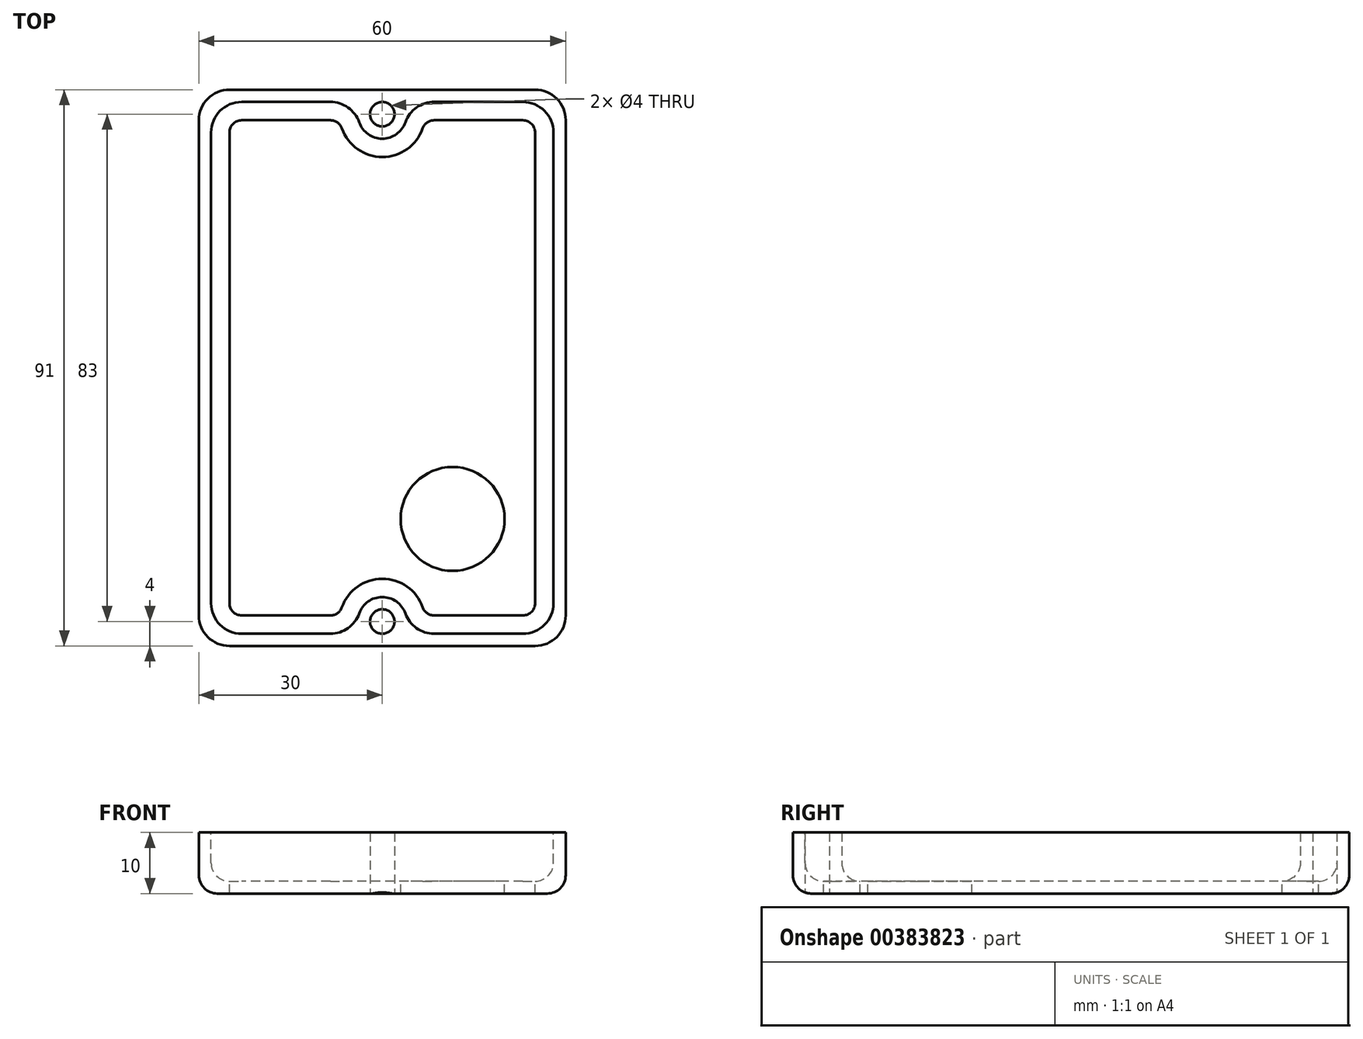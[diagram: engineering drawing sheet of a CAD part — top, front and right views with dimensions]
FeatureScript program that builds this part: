
annotation { "Feature Type Name" : "Feature", "Feature Type Description" : "" }
export const myFeature = defineFeature(function(context is Context, id is Id, definition is map)
    precondition{}
    {
        {
            assignVariable(context, id + "F0", {"name" : "lidwallthickness", "anyValue" : 2});
        }
        {
            assignVariable(context, id + "F1", {"name" : "lidheight", "anyValue" : 10});
        }
        {
            assignVariable(context, id + "F2", {"name" : "filletradius", "anyValue" : 3});
        }
        {
            var Q0;
            Q0=qCreatedBy(makeId("Top.planeOp"),FACE);
            var sketch = newSketch(context, id + "F3", { "sketchPlane" : qUnion([Q0])});
            skLineSegment(sketch, "E0.bottom", {"start": v(30, 45.5) * mm, "end": v(-30, 45.5) * mm});
            skLineSegment(sketch, "E0.top", {"start": v(30, -45.5) * mm, "end": v(-30, -45.5) * mm});
            skLineSegment(sketch, "E0.left", {"start": v(30, 45.5) * mm, "end": v(30, -45.5) * mm});
            skLineSegment(sketch, "E0.right", {"start": v(-30, 45.5) * mm, "end": v(-30, -45.5) * mm});
            skPoint(sketch, "E0.middle", {"position": v(0, 0) * mm});
            skSolve(sketch);
        }
        {
            var Q0;
            Q0=qSketchRegion(id+"F3",true);
            extrude(context, id + "F4", {"entities" : qUnion([Q0]), "depth" : (getVariable(context, 'lidheight')) * mm});
        }
        {
            var Q0;
            Q0=makeQuery(id+"F4.opExtrude","CAP_FACE",FACE,{"disambiguationData":[OSD([sQuery(id+"F3.wireOp",EDGE,"E0.bottom"),sQuery(id+"F3.wireOp",EDGE,"E0.top"),sQuery(id+"F3.wireOp",EDGE,"E0.left"),sQuery(id+"F3.wireOp",EDGE,"E0.right")])],"isStart":false});
            var sketch = newSketch(context, id + "F5", { "sketchPlane" : qUnion([Q0])});
            skLineSegment(sketch, "E1.bottom", {"start": v(28, 43.5) * mm, "end": v(-28, 43.5) * mm});
            skLineSegment(sketch, "E1.top", {"start": v(28, -43.5) * mm, "end": v(-28, -43.5) * mm});
            skLineSegment(sketch, "E1.left", {"start": v(28, 43.5) * mm, "end": v(28, -43.5) * mm});
            skLineSegment(sketch, "E1.right", {"start": v(-28, 43.5) * mm, "end": v(-28, -43.5) * mm});
            skPoint(sketch, "E1.middle", {"position": v(0, 0) * mm});
            skLineSegment(sketch, "E2.bottom", {"start": v(-12, 32.02) * mm, "end": v(12, 32.02) * mm});
            skLineSegment(sketch, "E2.top", {"start": v(-12, 8.02) * mm, "end": v(12, 8.02) * mm});
            skLineSegment(sketch, "E2.left", {"start": v(-12, 32.02) * mm, "end": v(-12, 8.02) * mm});
            skLineSegment(sketch, "E2.right", {"start": v(12, 32.02) * mm, "end": v(12, 8.02) * mm});
            skPoint(sketch, "E2.middle", {"position": v(0, 20.02) * mm});
            skSolve(sketch);
        }
        {
            var Q0;
            Q0=qSketchRegion(id+"F5",true);
            extrude(context, id + "F6", {"entities" : qUnion([Q0]), "operationType" : NewBodyOperationType.REMOVE, "oppositeDirection" : true, "depth" : (getVariable(context, 'lidheight') - getVariable(context, 'lidwallthickness')) * mm});
        }
        {
            var Q0;
            Q0=makeQuery(id+"F4.opExtrude","CAP_FACE",FACE,{"disambiguationData":[OSD([sQuery(id+"F3.wireOp",EDGE,"E0.bottom"),sQuery(id+"F3.wireOp",EDGE,"E0.top"),sQuery(id+"F3.wireOp",EDGE,"E0.left"),sQuery(id+"F3.wireOp",EDGE,"E0.right")])],"isStart":true});
            var sketch = newSketch(context, id + "F7", { "sketchPlane" : qUnion([Q0])});
            skCircle(sketch, "E3", {"center": v(0, -41.5) * mm, "radius": 4 * mm});
            skCircle(sketch, "E4.MirrorC", {"center": v(0, 41.5) * mm, "radius": 4 * mm});
            skSolve(sketch);
        }
        {
            var Q0;
            Q0=qSketchRegion(id+"F7",true);
            extrude(context, id + "F8", {"entities" : qUnion([Q0]), "operationType" : NewBodyOperationType.ADD, "oppositeDirection" : true, "depth" : (getVariable(context, 'lidheight')) * mm});
        }
        {
            var Q0;
            Q0=makeQuery(id+"F4.opExtrude","CAP_FACE",FACE,{"disambiguationData":[OSD([sQuery(id+"F3.wireOp",EDGE,"E0.bottom"),sQuery(id+"F3.wireOp",EDGE,"E0.top"),sQuery(id+"F3.wireOp",EDGE,"E0.left"),sQuery(id+"F3.wireOp",EDGE,"E0.right")])],"isStart":true});
            var sketch = newSketch(context, id + "F9", { "sketchPlane" : qUnion([Q0])});
            skCircle(sketch, "E5", {"center": v(0, -41.5) * mm, "radius": 2 * mm});
            skPoint(sketch, "E5.centerSnap0", {"position": v(0, -45.5) * mm});
            skCircle(sketch, "E6.MirrorC", {"center": v(0, 41.5) * mm, "radius": 2 * mm});
            skSolve(sketch);
        }
        {
            var Q0;
            Q0=qSketchRegion(id+"F9",true);
            extrude(context, id + "F10", {"entities" : qUnion([Q0]), "operationType" : NewBodyOperationType.REMOVE, "endBound" : BoundingType.THROUGH_ALL, "oppositeDirection" : true, "depth" : 25 * mm});
        }
        {
            var Q0;
            Q0=makeQuery(id+"F8.boolean.opBoolean","INTERSECT",EDGE,{"disambiguationData":[OD(1.0)],"derivedFrom":[makeQuery(id+"F6.boolean.opBoolean","COPY",FACE,{"derivedFrom":makeQuery(id+"F6.opExtrude","SWEPT_FACE",FACE,{"disambiguationData":[OSD([sQuery(id+"F5.wireOp",EDGE,"E1.bottom")])]})}),makeQuery(id+"F8.opExtrude","SWEPT_FACE",FACE,{"disambiguationData":[OSD([sQuery(id+"F7.wireOp",EDGE,"E3")])]})]});
            var Q1;
            Q1=makeQuery(id+"F8.boolean.opBoolean","INTERSECT",EDGE,{"disambiguationData":[OD(0.0)],"derivedFrom":[makeQuery(id+"F6.boolean.opBoolean","COPY",FACE,{"derivedFrom":makeQuery(id+"F6.opExtrude","SWEPT_FACE",FACE,{"disambiguationData":[OSD([sQuery(id+"F5.wireOp",EDGE,"E1.bottom")])]})}),makeQuery(id+"F8.opExtrude","SWEPT_FACE",FACE,{"disambiguationData":[OSD([sQuery(id+"F7.wireOp",EDGE,"E3")])]})]});
            var Q2;
            Q2=makeQuery(id+"F8.boolean.opBoolean","INTERSECT",EDGE,{"disambiguationData":[OD(0.0)],"derivedFrom":[makeQuery(id+"F6.boolean.opBoolean","COPY",FACE,{"derivedFrom":makeQuery(id+"F6.opExtrude","SWEPT_FACE",FACE,{"disambiguationData":[OSD([sQuery(id+"F5.wireOp",EDGE,"E1.top")])]})}),makeQuery(id+"F8.opExtrude","SWEPT_FACE",FACE,{"disambiguationData":[OSD([sQuery(id+"F7.wireOp",EDGE,"E4.MirrorC")])]})]});
            var Q3;
            Q3=makeQuery(id+"F8.boolean.opBoolean","INTERSECT",EDGE,{"disambiguationData":[OD(1.0)],"derivedFrom":[makeQuery(id+"F6.boolean.opBoolean","COPY",FACE,{"derivedFrom":makeQuery(id+"F6.opExtrude","SWEPT_FACE",FACE,{"disambiguationData":[OSD([sQuery(id+"F5.wireOp",EDGE,"E1.top")])]})}),makeQuery(id+"F8.opExtrude","SWEPT_FACE",FACE,{"disambiguationData":[OSD([sQuery(id+"F7.wireOp",EDGE,"E4.MirrorC")])]})]});
            fillet(context, id + "F11", {"entities" : qUnion([Q0, Q1, Q2, Q3]), "radius" : 5 * mm, "tangentPropagation" : true, "allowEdgeOverflow" : false});
        }
        {
            var Q0;
            Q0=makeQuery(id+"F4.opExtrude","SWEPT_EDGE",EDGE,{"disambiguationData":[OSD([sQuery(id+"F3.wireOp",EDGE,"E0.top"),sQuery(id+"F3.wireOp",EDGE,"E0.left")])]});
            var Q1;
            Q1=makeQuery(id+"F4.opExtrude","SWEPT_EDGE",EDGE,{"disambiguationData":[OSD([sQuery(id+"F3.wireOp",EDGE,"E0.top"),sQuery(id+"F3.wireOp",EDGE,"E0.right")])]});
            var Q2;
            Q2=makeQuery(id+"F4.opExtrude","SWEPT_EDGE",EDGE,{"disambiguationData":[OSD([sQuery(id+"F3.wireOp",EDGE,"E0.bottom"),sQuery(id+"F3.wireOp",EDGE,"E0.left")])]});
            var Q3;
            Q3=makeQuery(id+"F4.opExtrude","SWEPT_EDGE",EDGE,{"disambiguationData":[OSD([sQuery(id+"F3.wireOp",EDGE,"E0.bottom"),sQuery(id+"F3.wireOp",EDGE,"E0.right")])]});
            var Q4;
            Q4=makeQuery(id+"F6.boolean.opBoolean","COPY",EDGE,{"derivedFrom":makeQuery(id+"F6.opExtrude","SWEPT_EDGE",EDGE,{"disambiguationData":[OSD([sQuery(id+"F5.wireOp",EDGE,"E1.top"),sQuery(id+"F5.wireOp",EDGE,"E1.left")])]})});
            var Q5;
            Q5=makeQuery(id+"F6.boolean.opBoolean","COPY",EDGE,{"derivedFrom":makeQuery(id+"F6.opExtrude","SWEPT_EDGE",EDGE,{"disambiguationData":[OSD([sQuery(id+"F5.wireOp",EDGE,"E1.top"),sQuery(id+"F5.wireOp",EDGE,"E1.right")])]})});
            var Q6;
            Q6=makeQuery(id+"F6.boolean.opBoolean","COPY",EDGE,{"derivedFrom":makeQuery(id+"F6.opExtrude","SWEPT_EDGE",EDGE,{"disambiguationData":[OSD([sQuery(id+"F5.wireOp",EDGE,"E1.bottom"),sQuery(id+"F5.wireOp",EDGE,"E1.right")])]})});
            var Q7;
            Q7=makeQuery(id+"F6.boolean.opBoolean","COPY",EDGE,{"derivedFrom":makeQuery(id+"F6.opExtrude","SWEPT_EDGE",EDGE,{"disambiguationData":[OSD([sQuery(id+"F5.wireOp",EDGE,"E1.bottom"),sQuery(id+"F5.wireOp",EDGE,"E1.left")])]})});
            fillet(context, id + "F12", {"entities" : qUnion([Q0, Q1, Q2, Q3, Q4, Q5, Q6, Q7]), "radius" : 5 * mm, "tangentPropagation" : true, "allowEdgeOverflow" : false});
        }
        {
            var Q0;
            Q0=makeQuery(id+"F6.boolean.opBoolean","COPY",EDGE,{"derivedFrom":makeQuery(id+"F6.opExtrude","CAP_EDGE",EDGE,{"disambiguationData":[OSD([sQuery(id+"F5.wireOp",EDGE,"E1.right")])],"isStart":false})});
            var Q1;
            Q1=makeQuery(id+"F4.opExtrude","CAP_EDGE",EDGE,{"disambiguationData":[OSD([sQuery(id+"F3.wireOp",EDGE,"E0.left")])],"isStart":true});
            fillet(context, id + "F13", {"entities" : qUnion([Q0, Q1]), "radius" : (getVariable(context, 'filletradius')) * mm, "tangentPropagation" : true, "allowEdgeOverflow" : false});
        }
        {
            var Q0;
            Q0=makeQuery(id+"F6.boolean.opBoolean","COPY",FACE,{"derivedFrom":makeQuery(id+"F6.opExtrude","CAP_FACE",FACE,{"disambiguationData":[OSD([sQuery(id+"F5.wireOp",EDGE,"E1.bottom"),sQuery(id+"F5.wireOp",EDGE,"E1.top"),sQuery(id+"F5.wireOp",EDGE,"E1.left"),sQuery(id+"F5.wireOp",EDGE,"E1.right")])],"isStart":false})});
            var sketch = newSketch(context, id + "F14", { "sketchPlane" : qUnion([Q0])});
            skCircle(sketch, "E7", {"center": v(-11.5, -24.72) * mm, "radius": 8.5 * mm});
            skCircle(sketch, "E8.MirrorC", {"center": v(11.5, -24.72) * mm, "radius": 8.5 * mm});
            skSolve(sketch);
        }
        {
            var Q0;
            Q0=makeQuery(id+"F14.imprint","IMPRINT",FACE,{"disambiguationData":[TD([[makeQuery(id+"F14.imprint","IMPRINT",EDGE,{"derivedFrom":sQuery(id+"F14.wireOp",EDGE,"E8.MirrorC")}),-1.0]])]});
            var Q1;
            Q1=makeQuery(id+"F14.imprint","IMPRINT",FACE,{"disambiguationData":[TD([[makeQuery(id+"F14.imprint","IMPRINT",EDGE,{"derivedFrom":sQuery(id+"F14.wireOp",EDGE,"E7")}),1.0]])]});
            extrude(context, id + "F15", {"entities" : qUnion([Q0, Q1]), "operationType" : NewBodyOperationType.REMOVE, "endBound" : BoundingType.THROUGH_ALL, "oppositeDirection" : true, "depth" : 25 * mm});
        }
        {
            var Q0;
            Q0=makeQuery(id+"F6.boolean.opBoolean","SPLIT",FACE,{"disambiguationData":[TD([makeQuery(id+"F6.opExtrude","SWEPT_FACE",FACE,{"disambiguationData":[OSD([sQuery(id+"F5.wireOp",EDGE,"E2.bottom")])]})])],"derivedFrom":makeQuery(id+"F4.opExtrude","CAP_FACE",FACE,{"disambiguationData":[OSD([sQuery(id+"F3.wireOp",EDGE,"E0.bottom"),sQuery(id+"F3.wireOp",EDGE,"E0.top"),sQuery(id+"F3.wireOp",EDGE,"E0.left"),sQuery(id+"F3.wireOp",EDGE,"E0.right")])],"isStart":false})});
            extrude(context, id + "F16", {"entities" : qUnion([Q0]), "operationType" : NewBodyOperationType.REMOVE, "endBound" : BoundingType.THROUGH_ALL, "oppositeDirection" : true, "depth" : 25 * mm});
        }
    });
